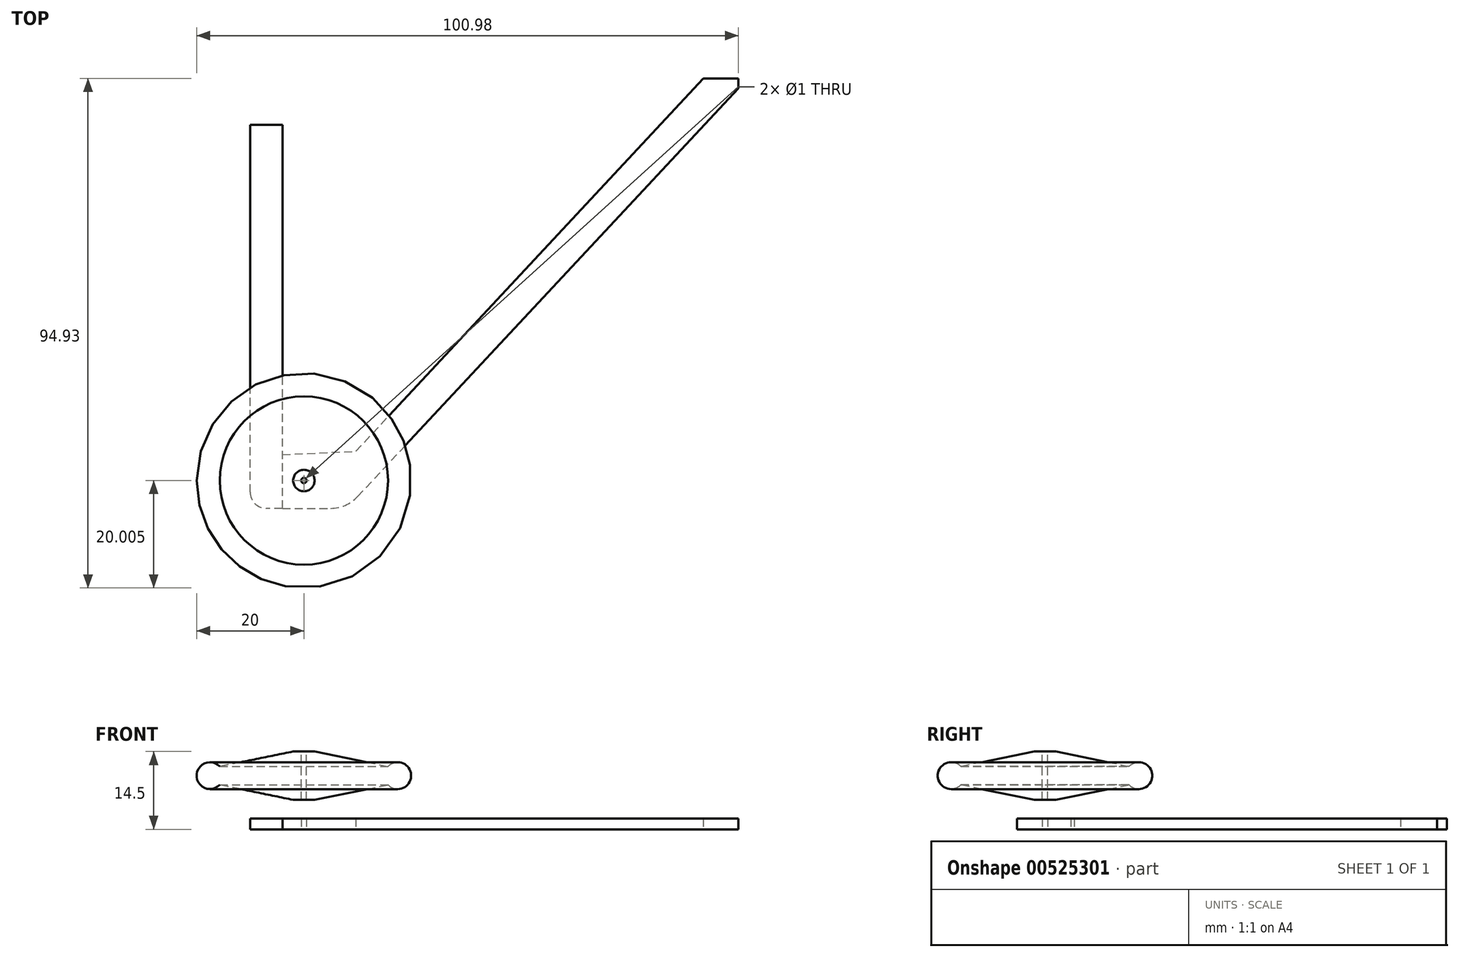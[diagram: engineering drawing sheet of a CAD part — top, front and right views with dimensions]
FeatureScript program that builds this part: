
annotation { "Feature Type Name" : "Feature", "Feature Type Description" : "" }
export const myFeature = defineFeature(function(context is Context, id is Id, definition is map)
    precondition{}
    {
        {
            var Q0;
            Q0=qCreatedBy(makeId("Top.planeOp"),FACE);
            var sketch = newSketch(context, id + "F0", { "sketchPlane" : qUnion([Q0])});
            skLineSegment(sketch, "E0", {"start": v(0, 0) * mm, "end": v(0, 71.5) * mm});
            skLineSegment(sketch, "E1", {"start": v(0, 0) * mm, "end": v(-3, 0) * mm});
            skArc(sketch, "E2", {"start": v(-6, 3) * mm, "mid": v(-5.12, 0.88) * mm, "end": v(-3, 0) * mm});
            skLineSegment(sketch, "E3", {"start": v(-6, 3) * mm, "end": v(-6, 71.5) * mm});
            skLineSegment(sketch, "E4", {"start": v(-6, 3) * mm, "end": v(-3, 3) * mm, "construction": true});
            skLineSegment(sketch, "E5", {"start": v(-3, 3) * mm, "end": v(0, 3) * mm, "construction": true});
            skLineSegment(sketch, "E6", {"start": v(-6, 71.5) * mm, "end": v(0, 71.5) * mm});
            skLineSegment(sketch, "E7", {"start": v(0, 10) * mm, "end": v(13.69, 10.63) * mm});
            skLineSegment(sketch, "E8", {"start": v(13.69, 10.63) * mm, "end": v(78.48, 80.11) * mm});
            skLineSegment(sketch, "E9", {"start": v(0, 0) * mm, "end": v(9, 0) * mm});
            skArc(sketch, "E10", {"start": v(9, 0) * mm, "mid": v(11.73, 0.57) * mm, "end": v(14, 2.18) * mm});
            skLineSegment(sketch, "E11", {"start": v(14, 2.18) * mm, "end": v(84.98, 78.28) * mm});
            skLineSegment(sketch, "E12", {"start": v(84.98, 78.28) * mm, "end": v(84.98, 80.11) * mm});
            skLineSegment(sketch, "E13", {"start": v(84.98, 80.11) * mm, "end": v(78.48, 80.11) * mm});
            skLineSegment(sketch, "E14", {"start": v(0, 5.18) * mm, "end": v(4, 5.18) * mm, "construction": true});
            skCircle(sketch, "E15", {"center": v(4, 5.18) * mm, "radius": 0.5 * mm});
            skLineSegment(sketch, "E16", {"start": v(4, 5.18) * mm, "end": v(4, 10.18) * mm, "construction": true});
            skSolve(sketch);
        }
        {
            var Q0;
            {var subQ1=sQuery(id+"F0.wireOp",EDGE,"E7");Q0=makeQuery(id+"F0.imprint","IMPRINT",FACE,{"disambiguationData":[TD([[makeQuery(id+"F0.imprint","IMPRINT",EDGE,{"derivedFrom":subQ1}),-1.0]])]});}
            extrude(context, id + "F1", {"entities" : qUnion([Q0]), "depth" : 2 * mm, "offsetDistance" : 25 * mm});
        }
        {
            var Q0;
            {var subQ0=sQuery(id+"F0.wireOp",EDGE,"E1");Q0=makeQuery(id+"F0.imprint","IMPRINT",FACE,{"disambiguationData":[TD([[makeQuery(id+"F0.imprint","IMPRINT",EDGE,{"derivedFrom":subQ0}),-1.0]])]});}
            extrude(context, id + "F2", {"entities" : qUnion([Q0]), "depth" : 2 * mm, "offsetDistance" : 25 * mm});
        }
        {
            var Q0;
            Q0=qCreatedBy(makeId("Top.planeOp"),FACE);
            var sketch = newSketch(context, id + "F3", { "sketchPlane" : qUnion([Q0])});
            skCircle(sketch, "E17", {"center": v(4, 5.18) * mm, "radius": 20 * mm});
            skSolve(sketch);
        }
        {
            var Q0;
            Q0=qCreatedBy(makeId("Right.planeOp"),FACE);
            var Q1;
            Q1=sQuery(id+"F0.wireOp",VERTEX,"E16.end");
            cPlane(context, id + "F4", {"entities" : qUnion([Q0, Q1]), "cplaneType" : CPlaneType.PLANE_POINT, "offset" : 25 * mm, "width" : 150 * mm, "height" : 150 * mm});
        }
        {
            var Q0;
            Q0=qCreatedBy(id+"F4.planeOp",FACE);
            var sketch = newSketch(context, id + "F5", { "sketchPlane" : qUnion([Q0])});
            skLineSegment(sketch, "E18", {"start": v(5.18, 0) * mm, "end": v(5.18, 10) * mm, "construction": true});
            skLineSegment(sketch, "E19", {"start": v(5.18, 10) * mm, "end": v(25.18, 10) * mm, "construction": true});
            skLineSegment(sketch, "E20", {"start": v(25.18, 10) * mm, "end": v(25.18, 0) * mm, "construction": true});
            skLineSegment(sketch, "E21", {"start": v(20.87, 8.28) * mm, "end": v(7.18, 5.5) * mm});
            skArc(sketch, "E22", {"start": v(20.87, 8.28) * mm, "mid": v(25.18, 10) * mm, "end": v(20.87, 11.72) * mm});
            skLineSegment(sketch, "E23.MirrorCS", {"start": v(20.87, 11.72) * mm, "end": v(7.18, 14.5) * mm});
            skLineSegment(sketch, "E24", {"start": v(7.18, 5.5) * mm, "end": v(5.18, 5.5) * mm});
            skLineSegment(sketch, "E25", {"start": v(5.18, 10) * mm, "end": v(5.18, 14.5) * mm, "construction": true});
            skLineSegment(sketch, "E26", {"start": v(5.18, 14.5) * mm, "end": v(7.18, 14.5) * mm});
            skLineSegment(sketch, "E27", {"start": v(5.18, 5.5) * mm, "end": v(5.18, 14.5) * mm});
            skSolve(sketch);
        }
        {
            var Q0;
            Q0=makeQuery(id+"F5.imprint","IMPRINT",FACE,{"disambiguationData":[TD([[makeQuery(id+"F5.imprint","IMPRINT",EDGE,{"derivedFrom":sQuery(id+"F5.wireOp",EDGE,"E21")}),-1.0]])]});
            var Q1;
            Q1=sQuery(id+"F5.wireOp",EDGE,"E27");
            revolve(context, id + "F6", {"entities" : qUnion([Q0]), "axis" : qUnion([Q1]), "revolveType" : RevolveType.FULL});
        }
        {
            var Q0;
            Q0=makeQuery(id+"F6.opRevolve","SWEPT_FACE",FACE,{"disambiguationData":[OSD([sQuery(id+"F5.wireOp",EDGE,"E26")])]});
            var sketch = newSketch(context, id + "F7", { "sketchPlane" : qUnion([Q0])});
            skCircle(sketch, "E28", {"center": v(4, 5.18) * mm, "radius": 0.5 * mm});
            skSolve(sketch);
        }
        {
            var Q0;
            Q0=makeQuery(id+"F7.imprint","IMPRINT",FACE,{"disambiguationData":[TD([[makeQuery(id+"F7.imprint","IMPRINT",EDGE,{"derivedFrom":sQuery(id+"F7.wireOp",EDGE,"E28")}),1.0]])]});
            extrude(context, id + "F8", {"entities" : qUnion([Q0]), "operationType" : NewBodyOperationType.REMOVE, "oppositeDirection" : true, "depth" : 25 * mm, "offsetDistance" : 25 * mm});
        }
    });
